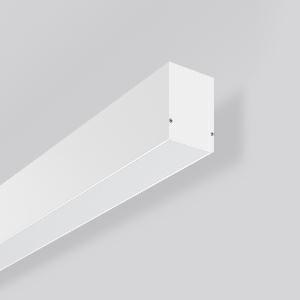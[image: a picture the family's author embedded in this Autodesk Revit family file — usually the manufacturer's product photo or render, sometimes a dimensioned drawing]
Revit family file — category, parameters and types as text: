
# Revit family: less_is_more_50_312610_002_9b6c
name_source: partatom
category: Lighting Fixtures
units: mm (PartAtom-declared; Revit-internal decimal feet)

## family parameters
Cut with Voids When Loaded = No
Host = Face
Light Source = No
Part Type = Normal
Room Calculation Point = No
Round Connector Dimension = Use Diameter
Shared = No

## types (1)
- LESS IS MORE 50 (1 x LED Modul 830, 3250 lm, 3000)
    Apparent Load = 25 VA
    CIE Flux Codes = 48 80 96 50 100
    Color Rendering = 80
    Color Temperature = 3000
    Default Elevation = 1800 mm
    Description = Series: LESS IS MORE 50
Linear wall luminaires. Housing: extruded aluminium profile, powder-coated. End cap aluminium powder-coated. Diffuser made of non-yellowing plastic (PMMA), opal. Direct 50%, indirect 50% light emission. Suitable for Wall (surface). LED unit with integrated converter interchangeable and removable. Suitable for through-wiring. With sensors or as a safety luminaire on request. 
Colour: traffic white, matt (RAL 9016)
Length: 1407 mm
Width: 67 mm
Height: 75 mm
Lamp: LED
Socket: without socket
Colour temperature: 3000K
Colour rendering index (CRI): 80
Light source: LED
Socket lamp2: Without base
Colour temperature: 3000K
Colour rendering index (CRI) 2: 80
System power: 25 W
Rated luminous flux: 3250 lm
Luminous efficiency: 130 lm/W
Control gear: Regulated power supply
Control gear: Regulated power supply
Protection class: I
Type of protection: IP 20
    Height = 75 mm
    Lamp = 1 x LED Modul 830
    Lamp Light Flux = 3250 lm
    Lamp count = 1
    Length = 1407 mm
    Lifetime = 50000 h
    Luminous efficacy = 130 lm/W
    Manufacturer = RZB
    ModVariant = No
    Model = 312610.002
    Mounting Place = Wall
    Mounting Type = Surface mounted
    Number of Poles = 1
    OnlyDefault = Yes
    Power Factor = 1
    Product Name = LESS IS MORE 50
    Product group = Surface mounted LED linear luminaires
    ProductGroupID = 2007
    Protection Class = Protection class I
    Protection Degree = IP 20
    RLX_Detail_Level = 1
    RLX_Emergency_Light_Flux = 0 lm
    RLX_Emergency_Type = 0
    RLX_Emergency_Type_DB = No
    RlxData = <blob elided: 39625 chars, md5=5249f869>
    Socket = socket
    Standby Power = 0 W
    System Light Flux = 3250 lm
    System Power = 25 W
    Type Comments = Product without accessories
    Type Image = 312606.002.jpg
    URL = http://relux.com
    VarID = ---
    Voltage = 0 V
    Weight = 0.00 kg
    Width = 67 mm

## geometry (parser evidence)
native form markers: Blend x4, Sweep x14
no freeform markers — native parametric forms only
